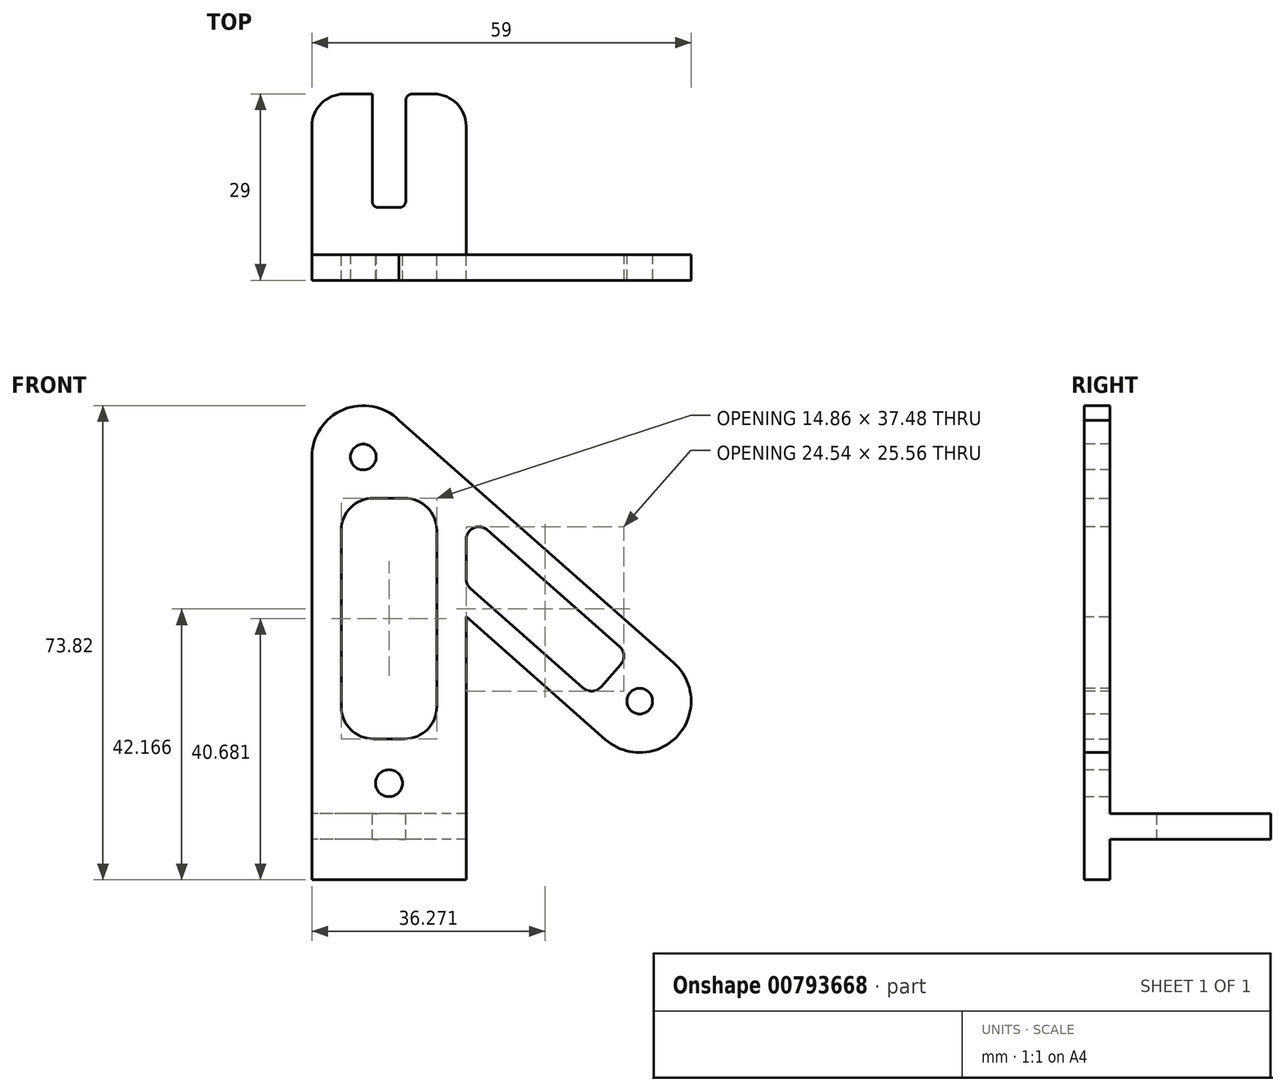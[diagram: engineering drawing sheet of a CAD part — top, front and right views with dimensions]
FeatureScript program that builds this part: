
annotation { "Feature Type Name" : "Feature", "Feature Type Description" : "" }
export const myFeature = defineFeature(function(context is Context, id is Id, definition is map)
    precondition{}
    {
        {
            var Q0;
            Q0=qCreatedBy(makeId("Front.planeOp"),FACE);
            var sketch = newSketch(context, id + "F0", { "sketchPlane" : qUnion([Q0])});
            skArc(sketch, "E0", {"start": v(-15.92, 24.74) * mm, "mid": v(-24.61, 26.37) * mm, "end": v(-29.5, 19) * mm});
            skArc(sketch, "E1", {"start": v(16.2, -25) * mm, "mid": v(27.5, -24.3) * mm, "end": v(26.8, -13) * mm});
            skLineSegment(sketch, "E2", {"start": v(-15.92, 24.74) * mm, "end": v(26.8, -13) * mm});
            skLineSegment(sketch, "E3", {"start": v(16.2, -25) * mm, "end": v(26.8, -13) * mm});
            skLineSegment(sketch, "E4", {"start": v(16.2, -25) * mm, "end": v(-5.5, -5.82) * mm});
            skLineSegment(sketch, "E5", {"start": v(-5.5, -5.82) * mm, "end": v(-5.5, -46.82) * mm});
            skLineSegment(sketch, "E6", {"start": v(-5.5, -46.82) * mm, "end": v(-29.5, -46.82) * mm});
            skLineSegment(sketch, "E7", {"start": v(-29.5, -46.82) * mm, "end": v(-29.5, 19) * mm});
            skSolve(sketch);
        }
        {
            var Q0;
            Q0 = qSketchRegion(id + "F0", true);
            extrude(context, id + "F1", {"entities" : qUnion([Q0]), "depth" : 4 * mm, "offsetDistance" : 25 * mm});
        }
        {
            var Q0;
            Q0=makeQuery(id+"F1.opExtrude","CAP_FACE",FACE,{"disambiguationData":[OSD([sQuery(id+"F0.wireOp",EDGE,"E0"),sQuery(id+"F0.wireOp",EDGE,"E1"),sQuery(id+"F0.wireOp",EDGE,"E2"),sQuery(id+"F0.wireOp",EDGE,"E4"),sQuery(id+"F0.wireOp",EDGE,"E5"),sQuery(id+"F0.wireOp",EDGE,"E6"),sQuery(id+"F0.wireOp",EDGE,"E7")])],"isStart":false});
            var sketch = newSketch(context, id + "F2", { "sketchPlane" : qUnion([Q0])});
            skCircle(sketch, "E8", {"center": v(-21.5, 19) * mm, "radius": 2 * mm});
            skCircle(sketch, "E9", {"center": v(21.5, -19) * mm, "radius": 2 * mm});
            skSolve(sketch);
        }
        {
            var Q0;
            Q0 = qSketchRegion(id + "F2", true);
            extrude(context, id + "F3", {"entities" : qUnion([Q0]), "operationType" : NewBodyOperationType.REMOVE, "oppositeDirection" : true, "depth" : 25 * mm, "offsetDistance" : 25 * mm});
        }
        {
            var Q0;
            Q0=makeQuery(id+"F1.opExtrude","CAP_FACE",FACE,{"disambiguationData":[OSD([sQuery(id+"F0.wireOp",EDGE,"E0"),sQuery(id+"F0.wireOp",EDGE,"E1"),sQuery(id+"F0.wireOp",EDGE,"E2"),sQuery(id+"F0.wireOp",EDGE,"E4"),sQuery(id+"F0.wireOp",EDGE,"E5"),sQuery(id+"F0.wireOp",EDGE,"E6"),sQuery(id+"F0.wireOp",EDGE,"E7")])],"isStart":true});
            var sketch = newSketch(context, id + "F4", { "sketchPlane" : qUnion([Q0])});
            skLineSegment(sketch, "E10.bottom", {"start": v(5.5, -36.5) * mm, "end": v(29.5, -36.5) * mm});
            skLineSegment(sketch, "E10.top", {"start": v(5.5, -40.5) * mm, "end": v(29.5, -40.5) * mm});
            skLineSegment(sketch, "E10.left", {"start": v(5.5, -36.5) * mm, "end": v(5.5, -40.5) * mm});
            skLineSegment(sketch, "E10.right", {"start": v(29.5, -36.5) * mm, "end": v(29.5, -40.5) * mm});
            skSolve(sketch);
        }
        {
            var Q0;
            Q0 = qSketchRegion(id + "F4", true);
            extrude(context, id + "F5", {"entities" : qUnion([Q0]), "operationType" : NewBodyOperationType.ADD, "depth" : 25 * mm, "offsetDistance" : 25 * mm});
        }
        {
            var Q0;
            Q0=makeQuery(id+"F5.opExtrude","SWEPT_FACE",FACE,{"disambiguationData":[OSD([sQuery(id+"F4.wireOp",EDGE,"E10.bottom")])]});
            var sketch = newSketch(context, id + "F6", { "sketchPlane" : qUnion([Q0])});
            skLineSegment(sketch, "E11.bottom", {"start": v(-14.9, 25) * mm, "end": v(-20.1, 25) * mm});
            skLineSegment(sketch, "E11.top", {"start": v(-14.9, 7.33) * mm, "end": v(-20.1, 7.33) * mm});
            skLineSegment(sketch, "E11.left", {"start": v(-14.9, 25) * mm, "end": v(-14.9, 7.33) * mm});
            skLineSegment(sketch, "E11.right", {"start": v(-20.1, 25) * mm, "end": v(-20.1, 7.33) * mm});
            skPoint(sketch, "E11.middle", {"position": v(-17.5, 16.17) * mm});
            skPoint(sketch, "E11.middle.positionSnap0", {"position": v(-17.5, 0) * mm});
            skPoint(sketch, "E11.centerSnap0", {"position": v(-17.5, 0) * mm});
            skSolve(sketch);
        }
        {
            var Q0;
            Q0 = qSketchRegion(id + "F6", true);
            extrude(context, id + "F7", {"entities" : qUnion([Q0]), "operationType" : NewBodyOperationType.REMOVE, "oppositeDirection" : true, "depth" : 25 * mm, "offsetDistance" : 25 * mm});
        }
        {
            var Q0;
            Q0=makeQuery(id+"F7.boolean.opBoolean","COPY",EDGE,{"derivedFrom":makeQuery(id+"F7.opExtrude","SWEPT_EDGE",EDGE,{"disambiguationData":[OSD([sQuery(id+"F6.wireOp",EDGE,"E11.top"),sQuery(id+"F6.wireOp",EDGE,"E11.right")])]})});
            fillet(context, id + "F8", {"entities" : qUnion([Q0]), "radius" : 1 * mm, "tangentPropagation" : true, "allowEdgeOverflow" : false});
        }
        {
            var Q0;
            Q0=makeQuery(id+"F7.boolean.opBoolean","COPY",EDGE,{"derivedFrom":makeQuery(id+"F7.opExtrude","SWEPT_EDGE",EDGE,{"disambiguationData":[OSD([sQuery(id+"F6.wireOp",EDGE,"E11.top"),sQuery(id+"F6.wireOp",EDGE,"E11.left")])]})});
            var Q1;
            Q1=makeQuery(id+"F7.boolean.opBoolean","COPY",EDGE,{"derivedFrom":makeQuery(id+"F7.opExtrude","SWEPT_EDGE",EDGE,{"disambiguationData":[OSD([sQuery(id+"F6.wireOp",EDGE,"E11.bottom"),sQuery(id+"F6.wireOp",EDGE,"E11.left")])]})});
            var Q2;
            Q2=makeQuery(id+"F7.boolean.opBoolean","COPY",EDGE,{"derivedFrom":makeQuery(id+"F7.opExtrude","SWEPT_EDGE",EDGE,{"disambiguationData":[OSD([sQuery(id+"F6.wireOp",EDGE,"E11.bottom"),sQuery(id+"F6.wireOp",EDGE,"E11.right")])]})});
            fillet(context, id + "F9", {"entities" : qUnion([Q0, Q1, Q2]), "radius" : 1 * mm, "tangentPropagation" : true, "allowEdgeOverflow" : false});
        }
        {
            var Q0;
            Q0=makeQuery(id+"F5.opExtrude","CAP_EDGE",EDGE,{"disambiguationData":[OSD([sQuery(id+"F4.wireOp",EDGE,"E10.left")])],"isStart":false});
            var Q1;
            Q1=makeQuery(id+"F5.opExtrude","CAP_EDGE",EDGE,{"disambiguationData":[OSD([sQuery(id+"F4.wireOp",EDGE,"E10.right")])],"isStart":false});
            fillet(context, id + "F10", {"entities" : qUnion([Q0, Q1]), "radius" : 5 * mm, "tangentPropagation" : true, "allowEdgeOverflow" : false});
        }
        {
            var Q0;
            {var subQ0=sQuery(id+"F0.wireOp",EDGE,"E7");var subQ1=sQuery(id+"F0.wireOp",EDGE,"E5");var subQ2=sQuery(id+"F0.wireOp",EDGE,"E0");var subQ3=sQuery(id+"F0.wireOp",EDGE,"E4");var subQ4=sQuery(id+"F0.wireOp",EDGE,"E1");var subQ5=sQuery(id+"F0.wireOp",EDGE,"E2");Q0=makeQuery(id+"F5.boolean.opBoolean","SPLIT",FACE,{"disambiguationData":[TD([makeQuery(id+"F1.opExtrude","SWEPT_FACE",FACE,{"disambiguationData":[OSD([subQ2])]})])],"derivedFrom":makeQuery(id+"F1.opExtrude","CAP_FACE",FACE,{"disambiguationData":[OSD([subQ2,subQ4,subQ5,subQ3,subQ1,sQuery(id+"F0.wireOp",EDGE,"E6"),subQ0])],"isStart":true})});}
            var sketch = newSketch(context, id + "F11", { "sketchPlane" : qUnion([Q0])});
            skLineSegment(sketch, "E12.bottom", {"start": v(24.93, 12.6) * mm, "end": v(10.07, 12.6) * mm});
            skLineSegment(sketch, "E12.top", {"start": v(24.93, -24.88) * mm, "end": v(10.07, -24.88) * mm});
            skLineSegment(sketch, "E12.left", {"start": v(24.93, 12.6) * mm, "end": v(24.93, -24.88) * mm});
            skLineSegment(sketch, "E12.right", {"start": v(10.07, 12.6) * mm, "end": v(10.07, -24.88) * mm});
            skPoint(sketch, "E12.middle", {"position": v(17.5, -6.14) * mm});
            skPoint(sketch, "E12.middle.positionSnap0", {"position": v(17.5, -36.5) * mm});
            skPoint(sketch, "E12.centerSnap0", {"position": v(17.5, -36.5) * mm});
            skLineSegment(sketch, "E13", {"start": v(-19.87, -11.83) * mm, "end": v(5.5, 10.58) * mm});
            skPoint(sketch, "E13.endSnap0", {"position": v(5.5, -21.16) * mm});
            skLineSegment(sketch, "E14", {"start": v(5.5, 10.58) * mm, "end": v(5.5, -0.86) * mm});
            skLineSegment(sketch, "E15", {"start": v(5.5, -0.86) * mm, "end": v(-14.2, -18.26) * mm});
            skLineSegment(sketch, "E16", {"start": v(-14.2, -18.26) * mm, "end": v(-19.87, -11.83) * mm});
            skLineSegment(sketch, "E17", {"start": v(-17.03, -15.05) * mm, "end": v(5.5, 4.86) * mm});
            skSolve(sketch);
        }
        {
            var Q0;
            Q0 = qSketchRegion(id + "F11", true);
            extrude(context, id + "F12", {"entities" : qUnion([Q0]), "operationType" : NewBodyOperationType.REMOVE, "endBound" : BoundingType.UP_TO_NEXT, "oppositeDirection" : true, "depth" : 25 * mm, "offsetDistance" : 25 * mm});
        }
        {
            var Q0;
            Q0 = qSketchRegion(id + "F11", true);
            extrude(context, id + "F13", {"entities" : qUnion([Q0]), "operationType" : NewBodyOperationType.REMOVE, "oppositeDirection" : true, "depth" : 25 * mm, "offsetDistance" : 25 * mm});
        }
        {
            var Q0;
            {var subQ0=sQuery(id+"F0.wireOp",EDGE,"E7");var subQ1=sQuery(id+"F0.wireOp",EDGE,"E5");var subQ2=sQuery(id+"F0.wireOp",EDGE,"E0");var subQ3=sQuery(id+"F0.wireOp",EDGE,"E4");var subQ4=sQuery(id+"F0.wireOp",EDGE,"E1");var subQ5=sQuery(id+"F0.wireOp",EDGE,"E2");Q0=makeQuery(id+"F5.boolean.opBoolean","SPLIT",FACE,{"disambiguationData":[TD([makeQuery(id+"F1.opExtrude","SWEPT_FACE",FACE,{"disambiguationData":[OSD([subQ2])]})])],"derivedFrom":makeQuery(id+"F1.opExtrude","CAP_FACE",FACE,{"disambiguationData":[OSD([subQ2,subQ4,subQ5,subQ3,subQ1,sQuery(id+"F0.wireOp",EDGE,"E6"),subQ0])],"isStart":true})});}
            var sketch = newSketch(context, id + "F14", { "sketchPlane" : qUnion([Q0])});
            skCircle(sketch, "E18", {"center": v(17.5, -31.77) * mm, "radius": 2.1 * mm});
            skPoint(sketch, "E18.centerSnap0", {"position": v(17.5, -36.5) * mm});
            skSolve(sketch);
        }
        {
            var Q0;
            Q0 = qSketchRegion(id + "F14", true);
            extrude(context, id + "F15", {"entities" : qUnion([Q0]), "operationType" : NewBodyOperationType.REMOVE, "endBound" : BoundingType.UP_TO_NEXT, "oppositeDirection" : true, "depth" : 25 * mm, "offsetDistance" : 25 * mm});
        }
        {
            var Q0;
            Q0=makeQuery(id+"F12.boolean.opBoolean","COPY",EDGE,{"derivedFrom":makeQuery(id+"F12.opExtrude","SWEPT_EDGE",EDGE,{"disambiguationData":[OSD([sQuery(id+"F11.wireOp",EDGE,"E12.bottom"),sQuery(id+"F11.wireOp",EDGE,"E12.left")])]})});
            var Q1;
            Q1=makeQuery(id+"F12.boolean.opBoolean","COPY",EDGE,{"derivedFrom":makeQuery(id+"F12.opExtrude","SWEPT_EDGE",EDGE,{"disambiguationData":[OSD([sQuery(id+"F11.wireOp",EDGE,"E12.bottom"),sQuery(id+"F11.wireOp",EDGE,"E12.right")])]})});
            var Q2;
            Q2=makeQuery(id+"F12.boolean.opBoolean","COPY",EDGE,{"derivedFrom":makeQuery(id+"F12.opExtrude","SWEPT_EDGE",EDGE,{"disambiguationData":[OSD([sQuery(id+"F11.wireOp",EDGE,"E12.top"),sQuery(id+"F11.wireOp",EDGE,"E12.right")])]})});
            var Q3;
            Q3=makeQuery(id+"F12.boolean.opBoolean","COPY",EDGE,{"derivedFrom":makeQuery(id+"F12.opExtrude","SWEPT_EDGE",EDGE,{"disambiguationData":[OSD([sQuery(id+"F11.wireOp",EDGE,"E12.top"),sQuery(id+"F11.wireOp",EDGE,"E12.left")])]})});
            fillet(context, id + "F16", {"entities" : qUnion([Q0, Q1, Q2, Q3]), "radius" : 5 * mm, "tangentPropagation" : true, "allowEdgeOverflow" : false});
        }
        {
            var Q0;
            Q0=makeQuery(id+"F12.boolean.opBoolean","COPY",EDGE,{"derivedFrom":makeQuery(id+"F12.opExtrude","SWEPT_EDGE",EDGE,{"disambiguationData":[OSD([sQuery(id+"F11.wireOp",EDGE,"E15"),sQuery(id+"F11.wireOp",EDGE,"E16")])]})});
            var Q1;
            Q1=makeQuery(id+"F12.boolean.opBoolean","COPY",EDGE,{"derivedFrom":makeQuery(id+"F12.opExtrude","SWEPT_EDGE",EDGE,{"disambiguationData":[OSD([sQuery(id+"F11.wireOp",EDGE,"E13"),sQuery(id+"F11.wireOp",EDGE,"E16")])]})});
            var Q2;
            Q2=makeQuery(id+"F12.boolean.opBoolean","COPY",EDGE,{"derivedFrom":makeQuery(id+"F12.opExtrude","SWEPT_EDGE",EDGE,{"disambiguationData":[OSD([sQuery(id+"F11.wireOp",EDGE,"E14"),sQuery(id+"F11.wireOp",EDGE,"E15")])]})});
            var Q3;
            Q3=makeQuery(id+"F12.boolean.opBoolean","COPY",EDGE,{"derivedFrom":makeQuery(id+"F12.opExtrude","SWEPT_EDGE",EDGE,{"disambiguationData":[OSD([sQuery(id+"F11.wireOp",EDGE,"E13"),sQuery(id+"F11.wireOp",EDGE,"E14")])]})});
            fillet(context, id + "F17", {"entities" : qUnion([Q0, Q1, Q2, Q3]), "radius" : 2 * mm, "tangentPropagation" : true, "allowEdgeOverflow" : false});
        }
    });
